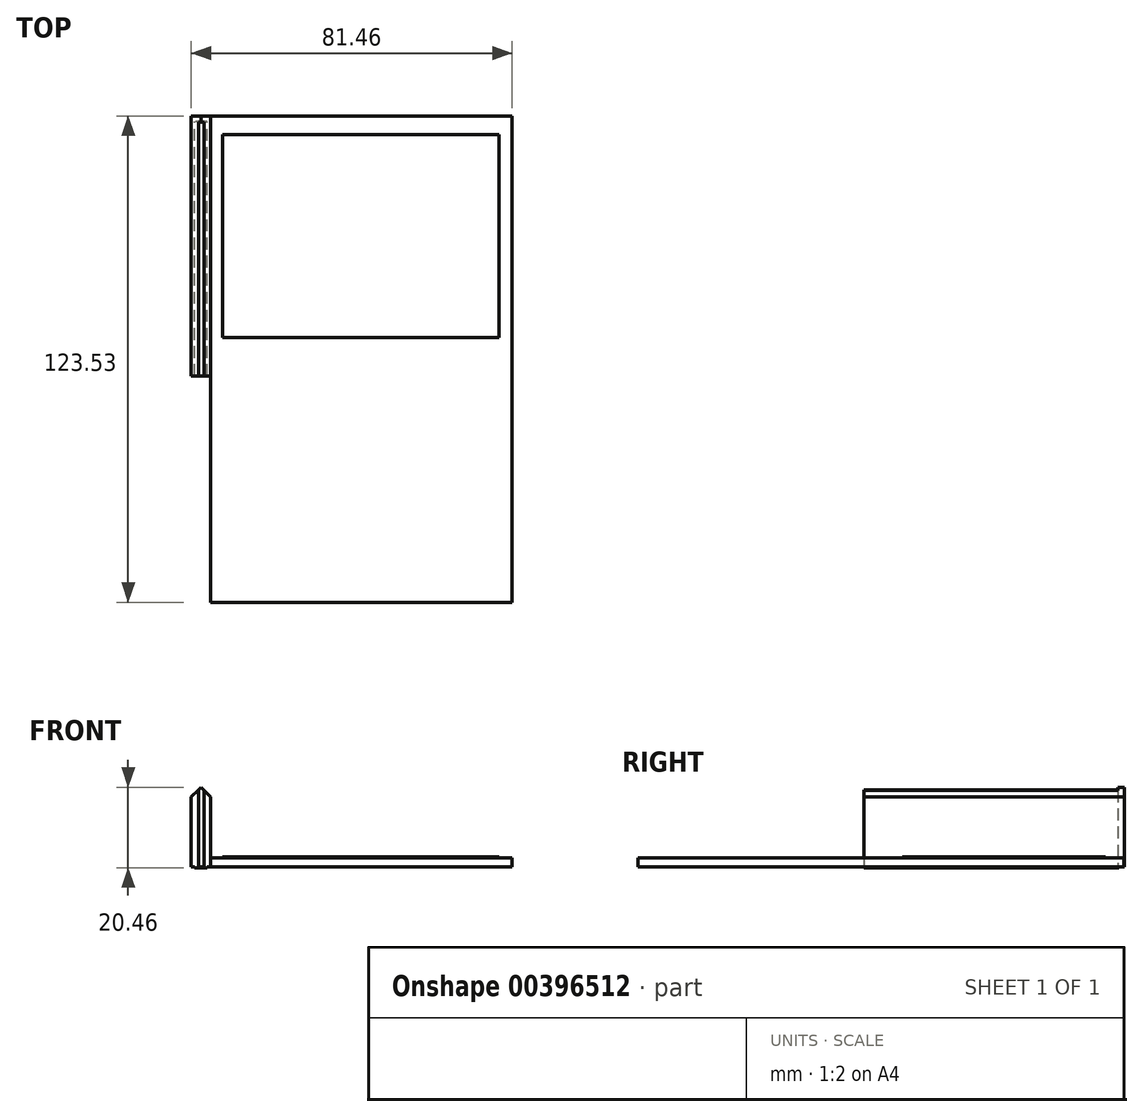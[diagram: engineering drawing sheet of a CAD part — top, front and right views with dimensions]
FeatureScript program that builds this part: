
annotation { "Feature Type Name" : "Feature", "Feature Type Description" : "" }
export const myFeature = defineFeature(function(context is Context, id is Id, definition is map)
    precondition{}
    {
        {
            var Q0;
            Q0=qCreatedBy(makeId("Top.planeOp"),FACE);
            var sketch = newSketch(context, id + "F0", { "sketchPlane" : qUnion([Q0])});
            skLineSegment(sketch, "E0.bottom", {"start": v(40.24, -57.48) * mm, "end": v(-36.3, -57.48) * mm});
            skLineSegment(sketch, "E0.top", {"start": v(40.24, 66) * mm, "end": v(-36.3, 66) * mm});
            skLineSegment(sketch, "E0.left", {"start": v(40.24, -57.48) * mm, "end": v(40.24, 66) * mm});
            skLineSegment(sketch, "E0.right", {"start": v(-36.3, -57.48) * mm, "end": v(-36.3, 66) * mm});
            skSolve(sketch);
        }
        {
            var Q0;
            Q0=makeQuery(id+"F0.imprint","IMPRINT",FACE,{"disambiguationData":[TD([[makeQuery(id+"F0.imprint","IMPRINT",EDGE,{"derivedFrom":sQuery(id+"F0.wireOp",EDGE,"E0.bottom")}),-1.0]])]});
            extrude(context, id + "F1", {"entities" : qUnion([Q0]), "depth" : 2.3 * mm});
        }
        {
            var Q0;
            Q0=qCreatedBy(makeId("Top.planeOp"),FACE);
            var sketch = newSketch(context, id + "F2", { "sketchPlane" : qUnion([Q0])});
            skLineSegment(sketch, "E1.bottom", {"start": v(-36.33, 66.05) * mm, "end": v(-41.22, 66.05) * mm});
            skLineSegment(sketch, "E1.top", {"start": v(-36.33, 0) * mm, "end": v(-41.22, 0) * mm});
            skLineSegment(sketch, "E1.left", {"start": v(-36.33, 66.05) * mm, "end": v(-36.33, 0) * mm});
            skLineSegment(sketch, "E1.right", {"start": v(-41.22, 66.05) * mm, "end": v(-41.22, 0) * mm});
            skLineSegment(sketch, "E2.bottom", {"start": v(-37.99, 0) * mm, "end": v(-39.43, 0) * mm});
            skLineSegment(sketch, "E2.top", {"start": v(-37.99, 64.51) * mm, "end": v(-39.43, 64.51) * mm});
            skLineSegment(sketch, "E2.left", {"start": v(-37.99, 0) * mm, "end": v(-37.99, 64.51) * mm});
            skLineSegment(sketch, "E2.right", {"start": v(-39.43, 0) * mm, "end": v(-39.43, 64.51) * mm});
            skSolve(sketch);
        }
        {
            var Q0;
            Q0=makeQuery(id+"F2.imprint","IMPRINT",FACE,{"disambiguationData":[TD([[makeQuery(id+"F2.imprint","IMPRINT",EDGE,{"derivedFrom":sQuery(id+"F2.wireOp",EDGE,"E1.bottom")}),1.0]])]});
            extrude(context, id + "F3", {"entities" : qUnion([Q0]), "depth" : 20.32 * mm});
        }
        {
            var Q0;
            Q0=qCreatedBy(makeId("Top.planeOp"),FACE);
            var sketch = newSketch(context, id + "F4", { "sketchPlane" : qUnion([Q0])});
            skLineSegment(sketch, "E3.bottom", {"start": v(-33.23, 61.3) * mm, "end": v(36.96, 61.3) * mm});
            skLineSegment(sketch, "E3.top", {"start": v(-33.23, 9.75) * mm, "end": v(36.96, 9.75) * mm});
            skLineSegment(sketch, "E3.left", {"start": v(-33.23, 61.3) * mm, "end": v(-33.23, 9.75) * mm});
            skLineSegment(sketch, "E3.right", {"start": v(36.96, 61.3) * mm, "end": v(36.96, 9.75) * mm});
            skSolve(sketch);
        }
        {
            var Q0;
            Q0 = qSketchRegion(id + "F4", true);
            extrude(context, id + "F5", {"entities" : qUnion([Q0]), "operationType" : NewBodyOperationType.ADD, "depth" : 2.54 * mm});
        }
        {
            var Q0;
            Q0=qCreatedBy(makeId("Top.planeOp"),FACE);
            var sketch = newSketch(context, id + "F6", { "sketchPlane" : qUnion([Q0])});
            skLineSegment(sketch, "E4.bottom", {"start": v(-37.17, 0) * mm, "end": v(-40.34, 0) * mm});
            skLineSegment(sketch, "E4.top", {"start": v(-37.17, 64.7) * mm, "end": v(-40.34, 64.7) * mm});
            skLineSegment(sketch, "E4.left", {"start": v(-37.17, 0) * mm, "end": v(-37.17, 64.7) * mm});
            skLineSegment(sketch, "E4.right", {"start": v(-40.34, 0) * mm, "end": v(-40.34, 64.7) * mm});
            skSolve(sketch);
        }
        {
            var Q0;
            Q0=makeQuery(id+"F6.imprint","IMPRINT",FACE,{"disambiguationData":[TD([[makeQuery(id+"F6.imprint","IMPRINT",EDGE,{"derivedFrom":sQuery(id+"F6.wireOp",EDGE,"E4.bottom")}),-1.0]])]});
            extrude(context, id + "F7", {"entities" : qUnion([Q0]), "operationType" : NewBodyOperationType.ADD, "oppositeDirection" : true, "depth" : 0.23 * mm});
        }
        {
            var Q0;
            Q0=makeQuery(id+"F3.opExtrude","CAP_EDGE",EDGE,{"disambiguationData":[OSD([sQuery(id+"F2.wireOp",EDGE,"E1.left")])],"isStart":false});
            var Q1;
            Q1=makeQuery(id+"F3.opExtrude","CAP_EDGE",EDGE,{"disambiguationData":[OSD([sQuery(id+"F2.wireOp",EDGE,"E1.right")])],"isStart":false});
            chamfer(context, id + "F8", {"entities" : qUnion([Q0, Q1]), "width" : 2.54 * mm, "tangentPropagation" : true});
        }
    });
